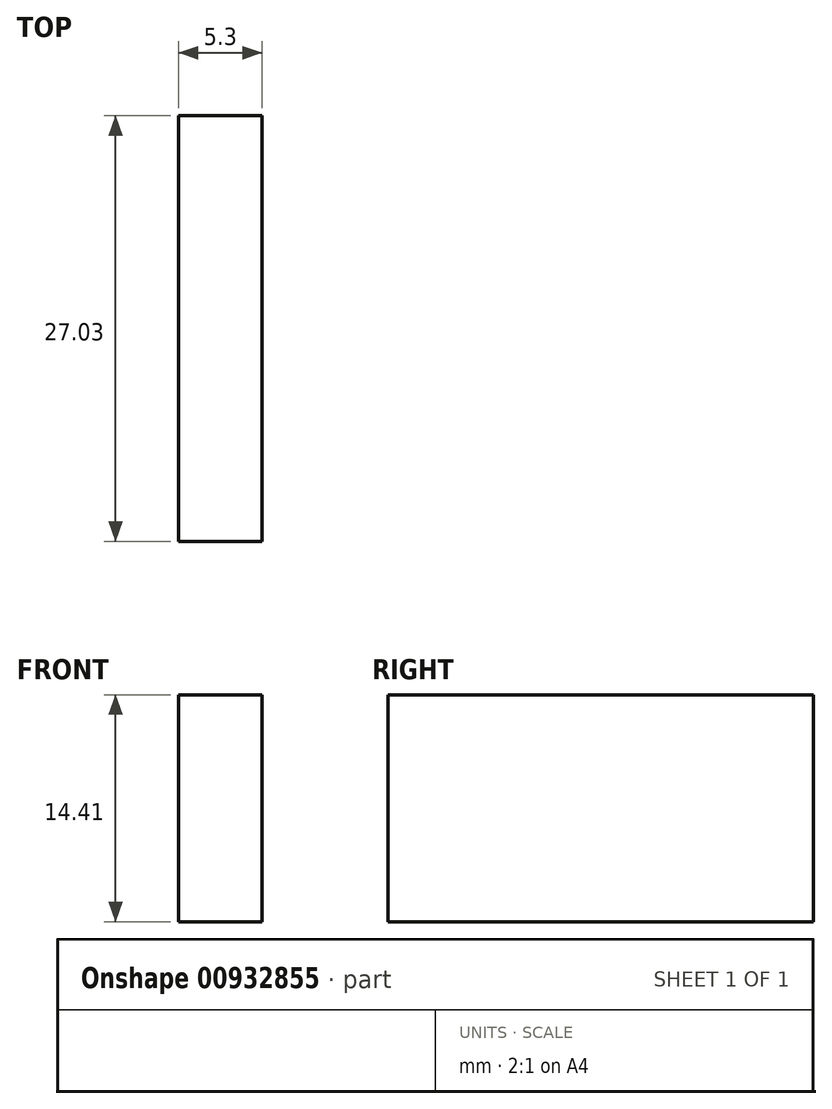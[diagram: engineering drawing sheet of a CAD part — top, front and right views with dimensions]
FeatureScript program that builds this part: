
annotation { "Feature Type Name" : "Feature", "Feature Type Description" : "" }
export const myFeature = defineFeature(function(context is Context, id is Id, definition is map)
    precondition{}
    {
        {
            var Q0;
            Q0=qCreatedBy(makeId("Front.planeOp"),FACE);
            var sketch = newSketch(context, id + "F0", { "sketchPlane" : qUnion([Q0])});
            skLineSegment(sketch, "E0.bottom", {"start": v(2.65, 18.56) * mm, "end": v(-2.65, 18.56) * mm});
            skLineSegment(sketch, "E0.top", {"start": v(2.65, 4.15) * mm, "end": v(-2.65, 4.15) * mm});
            skLineSegment(sketch, "E0.left", {"start": v(2.65, 18.56) * mm, "end": v(2.65, 4.15) * mm});
            skLineSegment(sketch, "E0.right", {"start": v(-2.65, 18.56) * mm, "end": v(-2.65, 4.15) * mm});
            skPoint(sketch, "E0.middle", {"position": v(0, 11.36) * mm});
            skSolve(sketch);
        }
        {
            var Q0;
            Q0=makeQuery(id+"F0.imprint","IMPRINT",FACE,{"disambiguationData":[TD([[makeQuery(id+"F0.imprint","IMPRINT",EDGE,{"derivedFrom":sQuery(id+"F0.wireOp",EDGE,"E0.bottom")}),1.0]])]});
            extrude(context, id + "F1", {"entities" : qUnion([Q0]), "depth" : 27.03 * mm, "offsetDistance" : 25.4 * mm});
        }
    });
